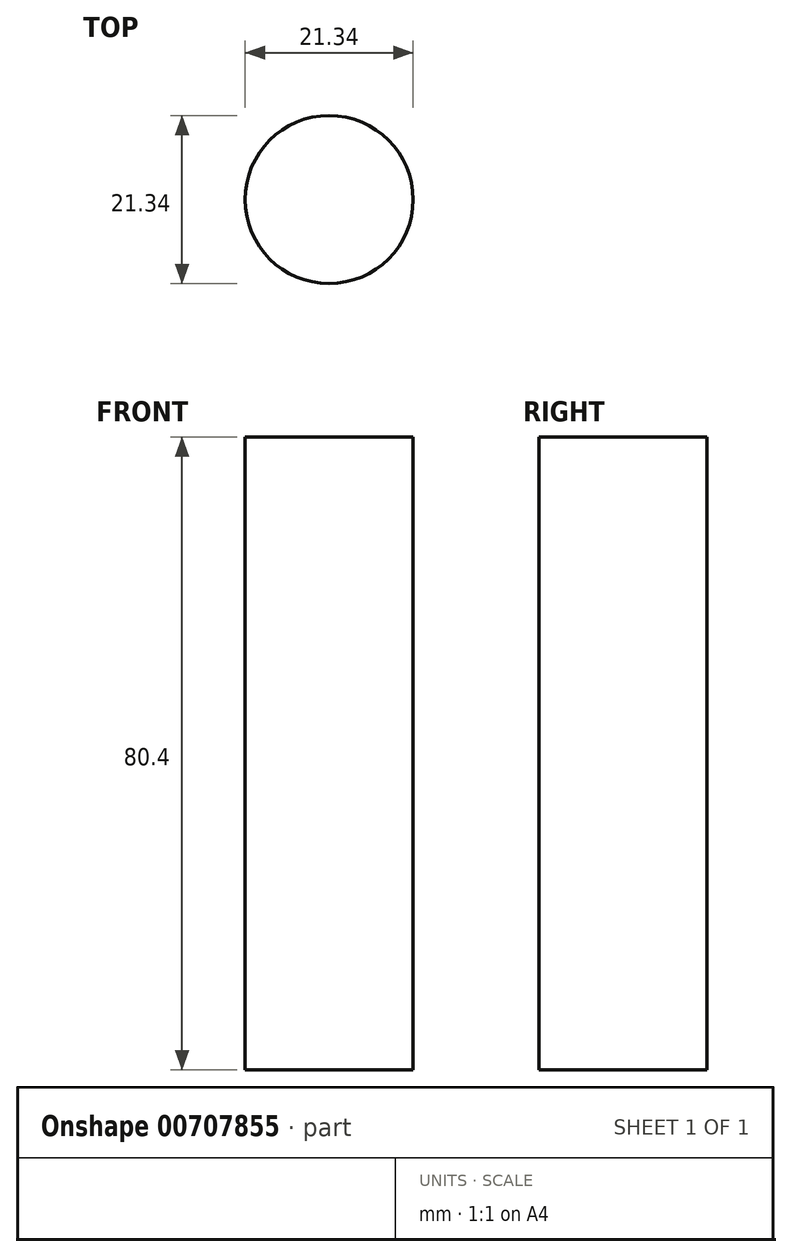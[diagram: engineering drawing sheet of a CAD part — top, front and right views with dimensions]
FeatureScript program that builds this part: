
annotation { "Feature Type Name" : "Feature", "Feature Type Description" : "" }
export const myFeature = defineFeature(function(context is Context, id is Id, definition is map)
    precondition{}
    {
        {
            var Q0;
            Q0=qCreatedBy(makeId("Top.planeOp"),FACE);
            var sketch = newSketch(context, id + "F0", { "sketchPlane" : qUnion([Q0])});
            skLineSegment(sketch, "E0.bottom", {"start": v(39.86, 22.34) * mm, "end": v(-39.86, 22.34) * mm});
            skLineSegment(sketch, "E0.top", {"start": v(39.86, -22.34) * mm, "end": v(-39.86, -22.34) * mm});
            skLineSegment(sketch, "E0.left", {"start": v(39.86, 22.34) * mm, "end": v(39.86, -22.34) * mm});
            skLineSegment(sketch, "E0.right", {"start": v(-39.86, 22.34) * mm, "end": v(-39.86, -22.34) * mm});
            skPoint(sketch, "E0.middle", {"position": v(0, 0) * mm});
            skCircle(sketch, "E1", {"center": v(0, 0) * mm, "radius": 10.67 * mm});
            skSolve(sketch);
        }
        {
            var Q0;
            Q0=makeQuery(id+"F0.imprint","IMPRINT",FACE,{"disambiguationData":[TD([[makeQuery(id+"F0.imprint","IMPRINT",EDGE,{"derivedFrom":sQuery(id+"F0.wireOp",EDGE,"E1")}),1.0]])]});
            extrude(context, id + "F1", {"entities" : qUnion([Q0]), "endBound" : BoundingType.SYMMETRIC, "depth" : 55.4 * mm, "offsetDistance" : 25 * mm});
        }
        {
            var Q0;
            Q0=makeQuery(id+"F1.opExtrude","CAP_FACE",FACE,{"disambiguationData":[OSD([sQuery(id+"F0.wireOp",EDGE,"E1")])],"isStart":false});
            extrude(context, id + "F2", {"entities" : qUnion([Q0]), "operationType" : NewBodyOperationType.ADD, "depth" : 25 * mm, "offsetDistance" : 25 * mm});
        }
    });
